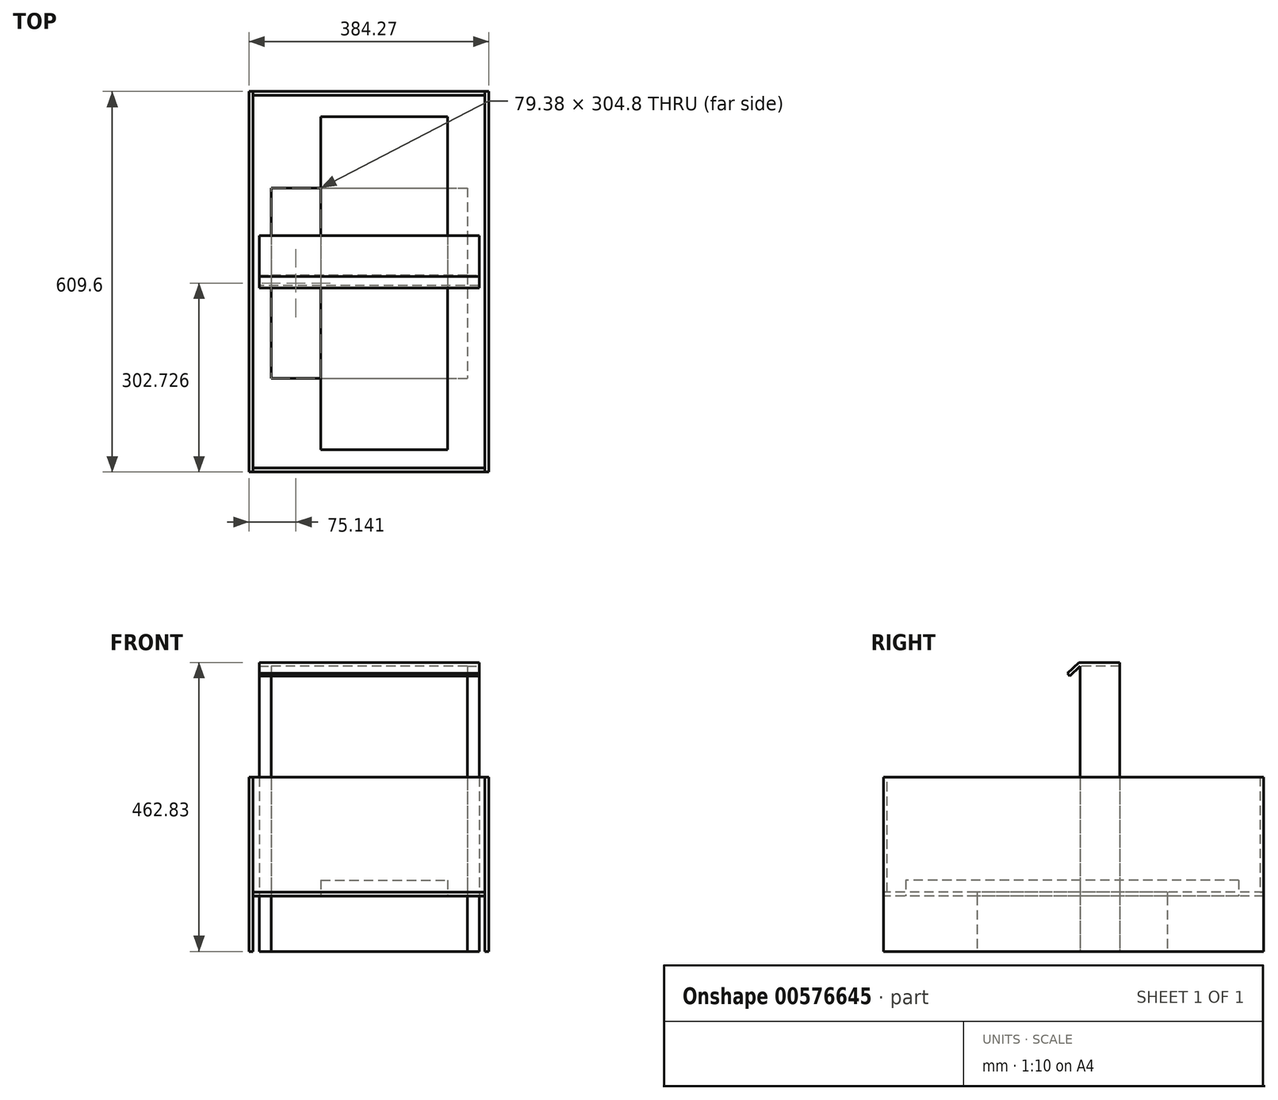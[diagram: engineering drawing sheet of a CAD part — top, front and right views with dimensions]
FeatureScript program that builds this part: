
annotation { "Feature Type Name" : "Feature", "Feature Type Description" : "" }
export const myFeature = defineFeature(function(context is Context, id is Id, definition is map)
    precondition{}
    {
        {
            var Q0;
            Q0=qCreatedBy(makeId("Top.planeOp"),FACE);
            var sketch = newSketch(context, id + "F0", { "sketchPlane" : qUnion([Q0])});
            skLineSegment(sketch, "E0.bottom", {"start": v(-153.08, 168.84) * mm, "end": v(161.25, 168.84) * mm});
            skLineSegment(sketch, "E0.top", {"start": v(-153.08, -135.96) * mm, "end": v(161.25, -135.96) * mm});
            skLineSegment(sketch, "E0.left", {"start": v(-153.08, 168.84) * mm, "end": v(-153.08, -135.96) * mm});
            skLineSegment(sketch, "E0.right", {"start": v(161.25, 168.84) * mm, "end": v(161.25, -135.96) * mm});
            skSolve(sketch);
        }
        {
            var Q0;
            Q0=makeQuery(id+"F0.imprint","IMPRINT",FACE,{"disambiguationData":[TD([[makeQuery(id+"F0.imprint","IMPRINT",EDGE,{"derivedFrom":sQuery(id+"F0.wireOp",EDGE,"E0.bottom")}),-1.0]])]});
            extrude(context, id + "F1", {"entities" : qUnion([Q0]), "depth" : 88.9 * mm, "offsetDistance" : 25.4 * mm});
        }
        {
            var Q0;
            Q0=makeQuery(id+"F1.opExtrude","CAP_FACE",FACE,{"disambiguationData":[OSD([sQuery(id+"F0.wireOp",EDGE,"E0.bottom"),sQuery(id+"F0.wireOp",EDGE,"E0.top"),sQuery(id+"F0.wireOp",EDGE,"E0.left"),sQuery(id+"F0.wireOp",EDGE,"E0.right")])],"isStart":false});
            var sketch = newSketch(context, id + "F2", { "sketchPlane" : qUnion([Q0])});
            skLineSegment(sketch, "E1.bottom", {"start": v(-73.7, 283.14) * mm, "end": v(129.5, 283.14) * mm});
            skLineSegment(sketch, "E1.top", {"start": v(-73.7, -250.26) * mm, "end": v(129.5, -250.26) * mm});
            skLineSegment(sketch, "E1.left", {"start": v(-73.7, 283.14) * mm, "end": v(-73.7, -250.26) * mm});
            skLineSegment(sketch, "E1.right", {"start": v(129.5, 283.14) * mm, "end": v(129.5, -250.26) * mm});
            skSolve(sketch);
        }
        {
            var Q0;
            {var subQ0=sQuery(id+"F2.wireOp",EDGE,"E1.bottom");Q0=makeQuery(id+"F2.imprint","IMPRINT",FACE,{"disambiguationData":[TD([[makeQuery(id+"F2.imprint","IMPRINT",EDGE,{"derivedFrom":subQ0}),-1.0]])]});}
            var Q1;
            {var subQ0=sQuery(id+"F2.wireOp",EDGE,"E1.left");var subQ1=makeQuery(id+"F1.opExtrude","CAP_EDGE",EDGE,{"disambiguationData":[OSD([sQuery(id+"F0.wireOp",EDGE,"E0.bottom")])],"isStart":false});var subQ2=makeQuery(id+"F2.imprint","INTERSECT",VERTEX,{"derivedFrom":[subQ1,subQ0]});Q1=makeQuery(id+"F2.imprint","IMPRINT",FACE,{"disambiguationData":[TD([[makeQuery(id+"F2.imprint","IMPRINT",EDGE,{"disambiguationData":[TD([[subQ2,-1.0]])],"derivedFrom":subQ0}),1.0]])]});}
            var Q2;
            {var subQ0=sQuery(id+"F2.wireOp",EDGE,"E1.top");Q2=makeQuery(id+"F2.imprint","IMPRINT",FACE,{"disambiguationData":[TD([[makeQuery(id+"F2.imprint","IMPRINT",EDGE,{"derivedFrom":subQ0}),1.0]])]});}
            extrude(context, id + "F3", {"entities" : qUnion([Q0, Q1, Q2]), "operationType" : NewBodyOperationType.ADD, "depth" : 25.4 * mm, "offsetDistance" : 25.4 * mm});
        }
        {
            var Q0;
            Q0=qCreatedBy(makeId("Top.planeOp"),FACE);
            var sketch = newSketch(context, id + "F4", { "sketchPlane" : qUnion([Q0])});
            skLineSegment(sketch, "E2.bottom", {"start": v(-172.13, 92.64) * mm, "end": v(-153.08, 92.64) * mm});
            skLineSegment(sketch, "E2.top", {"start": v(-172.13, 29.14) * mm, "end": v(-153.08, 29.14) * mm});
            skLineSegment(sketch, "E2.left", {"start": v(-172.13, 92.64) * mm, "end": v(-172.13, 29.14) * mm});
            skLineSegment(sketch, "E2.right", {"start": v(-153.08, 92.64) * mm, "end": v(-153.08, 29.14) * mm});
            skLineSegment(sketch, "E3.bottom", {"start": v(161.25, 92.64) * mm, "end": v(180.3, 92.64) * mm});
            skLineSegment(sketch, "E3.top", {"start": v(161.25, 29.14) * mm, "end": v(180.3, 29.14) * mm});
            skLineSegment(sketch, "E3.left", {"start": v(161.25, 92.64) * mm, "end": v(161.25, 29.14) * mm});
            skLineSegment(sketch, "E3.right", {"start": v(180.3, 92.64) * mm, "end": v(180.3, 29.14) * mm});
            skSolve(sketch);
        }
        {
            var Q0;
            Q0=makeQuery(id+"F4.imprint","IMPRINT",FACE,{"disambiguationData":[TD([[makeQuery(id+"F4.imprint","IMPRINT",EDGE,{"derivedFrom":sQuery(id+"F4.wireOp",EDGE,"E2.bottom")}),-1.0]])]});
            var Q1;
            Q1=makeQuery(id+"F4.imprint","IMPRINT",FACE,{"disambiguationData":[TD([[makeQuery(id+"F4.imprint","IMPRINT",EDGE,{"derivedFrom":sQuery(id+"F4.wireOp",EDGE,"E3.bottom")}),-1.0]])]});
            extrude(context, id + "F5", {"entities" : qUnion([Q0, Q1]), "operationType" : NewBodyOperationType.ADD, "depth" : 457.2 * mm, "offsetDistance" : 25.4 * mm});
        }
        {
            var Q0;
            Q0=makeQuery(id+"F5.opExtrude","SWEPT_FACE",FACE,{"disambiguationData":[OSD([sQuery(id+"F4.wireOp",EDGE,"E2.left")])]});
            var sketch = newSketch(context, id + "F6", { "sketchPlane" : qUnion([Q0])});
            skLineSegment(sketch, "E4", {"start": v(-92.64, 457.2) * mm, "end": v(-29.14, 457.2) * mm});
            skLineSegment(sketch, "E5", {"start": v(-29.14, 457.2) * mm, "end": v(-12.6, 441.15) * mm});
            skLineSegment(sketch, "E6", {"start": v(-12.6, 441.15) * mm, "end": v(-8.63, 445.25) * mm});
            skLineSegment(sketch, "E7", {"start": v(-8.63, 445.25) * mm, "end": v(-26.75, 462.83) * mm});
            skLineSegment(sketch, "E8", {"start": v(-26.75, 462.83) * mm, "end": v(-92.64, 462.83) * mm});
            skLineSegment(sketch, "E9", {"start": v(-92.64, 462.83) * mm, "end": v(-92.64, 457.2) * mm});
            skSolve(sketch);
        }
        {
            var Q0;
            Q0=makeQuery(id+"F6.imprint","IMPRINT",FACE,{"disambiguationData":[TD([[makeQuery(id+"F6.imprint","IMPRINT",EDGE,{"derivedFrom":sQuery(id+"F6.wireOp",EDGE,"E4")}),1.0]])]});
            extrude(context, id + "F7", {"entities" : qUnion([Q0]), "operationType" : NewBodyOperationType.ADD, "oppositeDirection" : true, "depth" : 352.42 * mm, "offsetDistance" : 25.4 * mm});
        }
        {
            var Q0;
            Q0=qCreatedBy(makeId("Top.planeOp"),FACE);
            var sketch = newSketch(context, id + "F8", { "sketchPlane" : qUnion([Q0])});
            skLineSegment(sketch, "E10.bottom", {"start": v(-188.53, 323.31) * mm, "end": v(-182.18, 323.31) * mm});
            skLineSegment(sketch, "E10.top", {"start": v(-188.53, -286.29) * mm, "end": v(-182.18, -286.29) * mm});
            skLineSegment(sketch, "E10.left", {"start": v(-188.53, 323.31) * mm, "end": v(-188.53, -286.29) * mm});
            skLineSegment(sketch, "E10.right", {"start": v(-182.18, 323.31) * mm, "end": v(-182.18, -286.29) * mm});
            skSolve(sketch);
        }
        {
            var Q0;
            Q0=makeQuery(id+"F8.imprint","IMPRINT",FACE,{"disambiguationData":[TD([[makeQuery(id+"F8.imprint","IMPRINT",EDGE,{"derivedFrom":sQuery(id+"F8.wireOp",EDGE,"E10.bottom")}),-1.0]])]});
            extrude(context, id + "F9", {"entities" : qUnion([Q0]), "depth" : 279.4 * mm, "offsetDistance" : 25.4 * mm});
        }
        {
            var Q0;
            {var subQ1=sQuery(id+"F0.wireOp",EDGE,"E0.left");var subQ2=sQuery(id+"F0.wireOp",EDGE,"E0.top");var subQ3=sQuery(id+"F0.wireOp",EDGE,"E0.bottom");Q0=makeQuery(id+"F3.boolean.opBoolean","SPLIT",FACE,{"disambiguationData":[TD([makeQuery(id+"F1.opExtrude","SWEPT_FACE",FACE,{"disambiguationData":[OSD([subQ1])]})])],"derivedFrom":makeQuery(id+"F1.opExtrude","CAP_FACE",FACE,{"disambiguationData":[OSD([subQ3,subQ2,subQ1,sQuery(id+"F0.wireOp",EDGE,"E0.right")])],"isStart":false})});}
            var sketch = newSketch(context, id + "F10", { "sketchPlane" : qUnion([Q0])});
            skLineSegment(sketch, "E11.bottom", {"start": v(-182.18, 323.31) * mm, "end": v(189.39, 323.31) * mm});
            skLineSegment(sketch, "E11.top", {"start": v(-182.18, -286.29) * mm, "end": v(189.39, -286.29) * mm});
            skLineSegment(sketch, "E11.left", {"start": v(-182.18, 323.31) * mm, "end": v(-182.18, -286.29) * mm});
            skLineSegment(sketch, "E11.right", {"start": v(189.39, 323.31) * mm, "end": v(189.39, -286.29) * mm});
            skSolve(sketch);
        }
        {
            var Q0;
            {var subQ13=sQuery(id+"F10.wireOp",EDGE,"E11.bottom");Q0=makeQuery(id+"F10.imprint","IMPRINT",FACE,{"disambiguationData":[TD([[makeQuery(id+"F10.imprint","IMPRINT",EDGE,{"derivedFrom":subQ13}),-1.0]])]});}
            var Q1;
            {var subQ1=sQuery(id+"F2.wireOp",EDGE,"E1.left");var subQ3=sQuery(id+"F0.wireOp",EDGE,"E0.left");var subQ4=sQuery(id+"F0.wireOp",EDGE,"E0.top");var subQ5=sQuery(id+"F0.wireOp",EDGE,"E0.bottom");var subQ6=makeQuery(id+"F1.opExtrude","CAP_FACE",FACE,{"disambiguationData":[OSD([subQ5,subQ4,subQ3,sQuery(id+"F0.wireOp",EDGE,"E0.right")])],"isStart":false});var subQ9=makeQuery(id+"F3.opExtrude","SWEPT_FACE",FACE,{"disambiguationData":[OSD([subQ1])]});var subQ15=makeQuery(id+"F3.boolean.opBoolean","SPLIT",EDGE,{"disambiguationData":[topologyDisambiguationEdgeConnected([subQ6,subQ9])],"derivedFrom":makeQuery(id+"F3.opExtrude","CAP_EDGE",EDGE,{"disambiguationData":[OSD([subQ1])],"isStart":true})});Q1=makeQuery(id+"F10.imprint","IMPRINT",FACE,{"disambiguationData":[TD([[makeQuery(id+"F10.imprint","IMPRINT",EDGE,{"derivedFrom":subQ15}),-1.0]])]});}
            extrude(context, id + "F11", {"entities" : qUnion([Q0, Q1]), "depth" : 6.35 * mm, "offsetDistance" : 25.4 * mm});
        }
        {
            var Q0;
            Q0=makeQuery(id+"F11.opExtrude","SWEPT_FACE",FACE,{"disambiguationData":[OSD([sQuery(id+"F10.wireOp",EDGE,"E11.top")])]});
            var sketch = newSketch(context, id + "F12", { "sketchPlane" : qUnion([Q0])});
            skLineSegment(sketch, "E12.bottom", {"start": v(-182.18, 95.25) * mm, "end": v(189.39, 95.25) * mm});
            skLineSegment(sketch, "E12.top", {"start": v(-182.18, 279.4) * mm, "end": v(189.39, 279.4) * mm});
            skLineSegment(sketch, "E12.left", {"start": v(-182.18, 95.25) * mm, "end": v(-182.18, 279.4) * mm});
            skLineSegment(sketch, "E12.right", {"start": v(189.39, 95.25) * mm, "end": v(189.39, 279.4) * mm});
            skSolve(sketch);
        }
        {
            var Q0;
            Q0=makeQuery(id+"F12.imprint","IMPRINT",FACE,{"disambiguationData":[TD([[makeQuery(id+"F12.imprint","IMPRINT",EDGE,{"derivedFrom":sQuery(id+"F12.wireOp",EDGE,"E12.top")}),-1.0]])]});
            extrude(context, id + "F13", {"entities" : qUnion([Q0]), "oppositeDirection" : true, "depth" : 6.35 * mm, "offsetDistance" : 25.4 * mm});
        }
        {
            var Q0;
            Q0=makeQuery(id+"F11.opExtrude","SWEPT_FACE",FACE,{"disambiguationData":[OSD([sQuery(id+"F10.wireOp",EDGE,"E11.right")])]});
            var sketch = newSketch(context, id + "F14", { "sketchPlane" : qUnion([Q0])});
            skLineSegment(sketch, "E13.bottom", {"start": v(-286.29, 279.4) * mm, "end": v(323.31, 279.4) * mm});
            skLineSegment(sketch, "E13.top", {"start": v(-286.29, 0) * mm, "end": v(323.31, 0) * mm});
            skLineSegment(sketch, "E13.left", {"start": v(-286.29, 279.4) * mm, "end": v(-286.29, 0) * mm});
            skLineSegment(sketch, "E13.right", {"start": v(323.31, 279.4) * mm, "end": v(323.31, 0) * mm});
            skSolve(sketch);
        }
        {
            var Q0;
            {var subQ0=sQuery(id+"F14.wireOp",EDGE,"E13.top");Q0=makeQuery(id+"F14.imprint","IMPRINT",FACE,{"disambiguationData":[TD([[makeQuery(id+"F14.imprint","IMPRINT",EDGE,{"derivedFrom":subQ0}),1.0]])]});}
            var Q1;
            {var subQ1=sQuery(id+"F10.wireOp",EDGE,"E11.right");var subQ2=makeQuery(id+"F11.opExtrude","CAP_EDGE",EDGE,{"disambiguationData":[OSD([subQ1])],"isStart":true});Q1=makeQuery(id+"F14.imprint","IMPRINT",FACE,{"disambiguationData":[TD([[makeQuery(id+"F14.imprint","IMPRINT",EDGE,{"derivedFrom":subQ2}),-1.0]])]});}
            var Q2;
            {var subQ0=sQuery(id+"F14.wireOp",EDGE,"E13.bottom");Q2=makeQuery(id+"F14.imprint","IMPRINT",FACE,{"disambiguationData":[TD([[makeQuery(id+"F14.imprint","IMPRINT",EDGE,{"derivedFrom":subQ0}),-1.0]])]});}
            extrude(context, id + "F15", {"entities" : qUnion([Q0, Q1, Q2]), "depth" : 6.35 * mm, "offsetDistance" : 25.4 * mm});
        }
        {
            var Q0;
            Q0=makeQuery(id+"F15.opExtrude","SWEPT_FACE",FACE,{"disambiguationData":[OSD([sQuery(id+"F14.wireOp",EDGE,"E13.right")])]});
            var sketch = newSketch(context, id + "F16", { "sketchPlane" : qUnion([Q0])});
            skLineSegment(sketch, "E14.bottom", {"start": v(-189.39, 279.4) * mm, "end": v(182.18, 279.4) * mm});
            skLineSegment(sketch, "E14.top", {"start": v(-189.39, 95.25) * mm, "end": v(182.18, 95.25) * mm});
            skLineSegment(sketch, "E14.left", {"start": v(-189.39, 279.4) * mm, "end": v(-189.39, 95.25) * mm});
            skLineSegment(sketch, "E14.right", {"start": v(182.18, 279.4) * mm, "end": v(182.18, 95.25) * mm});
            skSolve(sketch);
        }
        {
            var Q0;
            Q0=makeQuery(id+"F16.imprint","IMPRINT",FACE,{"disambiguationData":[TD([[makeQuery(id+"F16.imprint","IMPRINT",EDGE,{"derivedFrom":sQuery(id+"F16.wireOp",EDGE,"E14.bottom")}),-1.0]])]});
            extrude(context, id + "F17", {"entities" : qUnion([Q0]), "oppositeDirection" : true, "depth" : 6.35 * mm, "offsetDistance" : 25.4 * mm});
        }
    });
